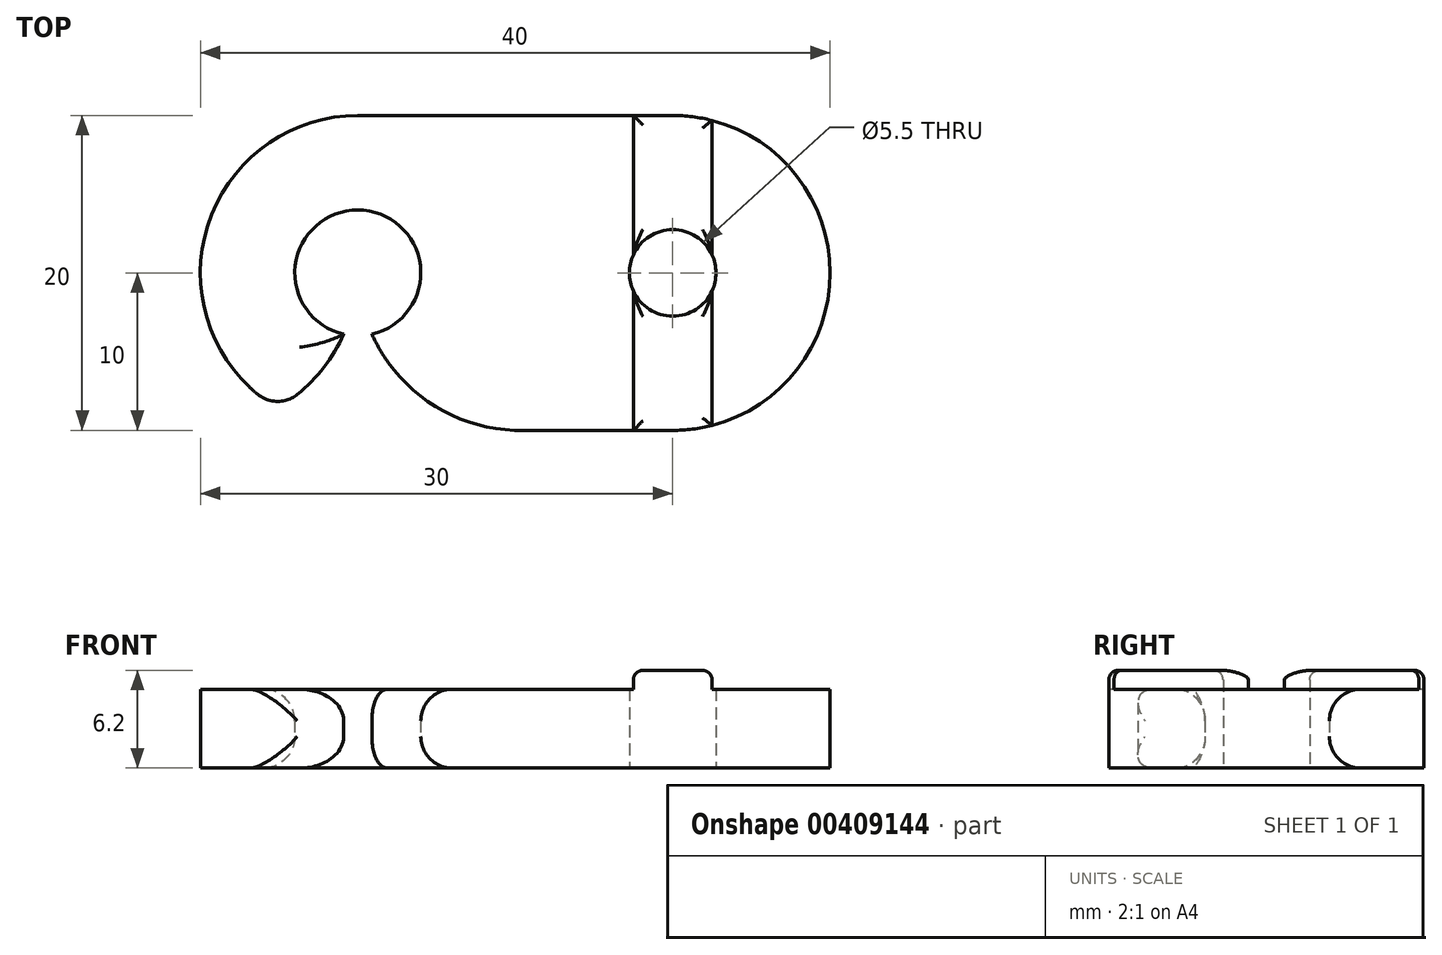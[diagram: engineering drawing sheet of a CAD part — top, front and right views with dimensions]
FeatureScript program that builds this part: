
annotation { "Feature Type Name" : "Feature", "Feature Type Description" : "" }
export const myFeature = defineFeature(function(context is Context, id is Id, definition is map)
    precondition{}
    {
        {
            var Q0;
            Q0=qCreatedBy(makeId("Top.planeOp"),FACE);
            var sketch = newSketch(context, id + "F0", { "sketchPlane" : qUnion([Q0])});
            skArc(sketch, "E0", {"start": v(10, -10) * mm, "mid": v(20, 0) * mm, "end": v(10, 10) * mm});
            skLineSegment(sketch, "E1", {"start": v(0, -10) * mm, "end": v(10, -10) * mm});
            skLineSegment(sketch, "E2", {"start": v(0, 10) * mm, "end": v(10, 10) * mm});
            skCircle(sketch, "E3", {"center": v(10, 0) * mm, "radius": 2.75 * mm});
            skArc(sketch, "E4.MirrorCS", {"start": v(-10, -10) * mm, "mid": v(-20, 0) * mm, "end": v(-10, 10) * mm});
            skLineSegment(sketch, "E5.MirrorCS", {"start": v(0, -10) * mm, "end": v(-10, -10) * mm});
            skCircle(sketch, "E6.MirrorC", {"center": v(-10, 0) * mm, "radius": 4 * mm});
            skLineSegment(sketch, "E7.MirrorCS", {"start": v(0, 10) * mm, "end": v(-10, 10) * mm});
            skLineSegment(sketch, "E8", {"start": v(-10, 0) * mm, "end": v(-10, -10) * mm, "construction": true});
            skLineSegment(sketch, "E9", {"start": v(-10, -3.9) * mm, "end": v(-9.1, -3.9) * mm, "construction": true});
            skArc(sketch, "E10", {"start": v(-10, 0) * mm, "mid": v(-6.98, -6.98) * mm, "end": v(0, -10) * mm});
            skArc(sketch, "E11.MirrorCS", {"start": v(-10, 0) * mm, "mid": v(-13.02, -6.98) * mm, "end": v(-20, -10) * mm});
            skSolve(sketch);
        }
        {
            var Q0;
            Q0=makeQuery(id+"F0.imprint","IMPRINT",FACE,{"disambiguationData":[TD([[makeQuery(id+"F0.imprint","IMPRINT",EDGE,{"derivedFrom":sQuery(id+"F0.wireOp",EDGE,"E0")}),1.0]])]});
            extrude(context, id + "F1", {"entities" : qUnion([Q0]), "depth" : 5 * mm, "offsetDistance" : 25 * mm});
        }
        {
            var Q0;
            Q0=makeQuery(id+"F1.opExtrude","CAP_FACE",FACE,{"disambiguationData":[OSD([sQuery(id+"F0.wireOp",EDGE,"E0"),sQuery(id+"F0.wireOp",EDGE,"E1"),sQuery(id+"F0.wireOp",EDGE,"E2"),sQuery(id+"F0.wireOp",EDGE,"E3"),sQuery(id+"F0.wireOp",EDGE,"E4.MirrorCS"),sQuery(id+"F0.wireOp",EDGE,"E6.MirrorC"),sQuery(id+"F0.wireOp",EDGE,"E7.MirrorCS"),sQuery(id+"F0.wireOp",EDGE,"E10"),sQuery(id+"F0.wireOp",EDGE,"E11.MirrorCS")])],"isStart":false});
            var sketch = newSketch(context, id + "F2", { "sketchPlane" : qUnion([Q0])});
            skCircle(sketch, "E12", {"center": v(10, 0) * mm, "radius": 2.5 * mm, "construction": true});
            skLineSegment(sketch, "E13", {"start": v(7.5, 10) * mm, "end": v(7.5, -10) * mm});
            skLineSegment(sketch, "E14", {"start": v(12.5, 9.68) * mm, "end": v(12.5, -9.68) * mm});
            skSolve(sketch);
        }
        {
            var Q0;
            {var subQ1=makeQuery(id+"F1.opExtrude","CAP_EDGE",EDGE,{"disambiguationData":[OSD([sQuery(id+"F0.wireOp",EDGE,"E0")])],"isStart":false});var subQ3=sQuery(id+"F2.wireOp",EDGE,"E14");var subQ4=makeQuery(id+"F2.imprint","INTERSECT",VERTEX,{"disambiguationData":[OD(0.0)],"derivedFrom":[subQ1,subQ3]});Q0=makeQuery(id+"F2.imprint","IMPRINT",FACE,{"disambiguationData":[TD([[makeQuery(id+"F2.imprint","IMPRINT",EDGE,{"disambiguationData":[TD([[subQ4,-1.0]])],"derivedFrom":subQ3}),-1.0]])]});}
            var Q1;
            {var subQ0=makeQuery(id+"F1.opExtrude","CAP_EDGE",EDGE,{"disambiguationData":[OSD([sQuery(id+"F0.wireOp",EDGE,"E1")])],"isStart":false});var subQ3=sQuery(id+"F2.wireOp",EDGE,"E13");var subQ4=makeQuery(id+"F2.imprint","INTERSECT",VERTEX,{"derivedFrom":[subQ0,subQ3]});Q1=makeQuery(id+"F2.imprint","IMPRINT",FACE,{"disambiguationData":[TD([[makeQuery(id+"F2.imprint","IMPRINT",EDGE,{"disambiguationData":[TD([[subQ4,1.0]])],"derivedFrom":subQ3}),1.0]])]});}
            extrude(context, id + "F3", {"entities" : qUnion([Q0, Q1]), "operationType" : NewBodyOperationType.ADD, "depth" : 1.2 * mm, "offsetDistance" : 25 * mm});
        }
        {
            var Q0;
            Q0=makeQuery(id+"F3.opExtrude","CAP_FACE",FACE,{"disambiguationData":[OSD([sQuery(id+"F0.wireOp",EDGE,"E0"),sQuery(id+"F0.wireOp",EDGE,"E2"),sQuery(id+"F0.wireOp",EDGE,"E3"),sQuery(id+"F0.wireOp",EDGE,"E7.MirrorCS"),sQuery(id+"F2.wireOp",EDGE,"E13"),sQuery(id+"F2.wireOp",EDGE,"E14")])],"isStart":false});
            var Q1;
            Q1=makeQuery(id+"F3.opExtrude","CAP_FACE",FACE,{"disambiguationData":[OSD([sQuery(id+"F0.wireOp",EDGE,"E0"),sQuery(id+"F0.wireOp",EDGE,"E1"),sQuery(id+"F0.wireOp",EDGE,"E3"),sQuery(id+"F2.wireOp",EDGE,"E13"),sQuery(id+"F2.wireOp",EDGE,"E14")])],"isStart":false});
            var Q2;
            {var subQ0=sQuery(id+"F2.wireOp",EDGE,"E13");Q2=makeQuery(id+"F3.opExtrude","CAP_EDGE",EDGE,{"disambiguationData":[OSD([subQ0]),TDD([makeQuery(id+"F2.imprint","IMPRINT",EDGE,{"disambiguationData":[TD([[makeQuery(id+"F2.imprint","INTERSECT",VERTEX,{"disambiguationData":[OD(0.0)],"derivedFrom":[makeQuery(id+"F1.opExtrude","CAP_EDGE",EDGE,{"disambiguationData":[OSD([sQuery(id+"F0.wireOp",EDGE,"E3")])],"isStart":false}),subQ0]}),1.0]])],"derivedFrom":subQ0})])],"isStart":true});}
            var Q3;
            {var subQ0=sQuery(id+"F2.wireOp",EDGE,"E14");Q3=makeQuery(id+"F3.opExtrude","CAP_EDGE",EDGE,{"disambiguationData":[OSD([subQ0]),TDD([makeQuery(id+"F2.imprint","IMPRINT",EDGE,{"disambiguationData":[TD([[makeQuery(id+"F2.imprint","INTERSECT",VERTEX,{"disambiguationData":[OD(0.0)],"derivedFrom":[makeQuery(id+"F1.opExtrude","CAP_EDGE",EDGE,{"disambiguationData":[OSD([sQuery(id+"F0.wireOp",EDGE,"E0")])],"isStart":false}),subQ0]}),-1.0]])],"derivedFrom":subQ0})])],"isStart":true});}
            fillet(context, id + "F4", {"entities" : qUnion([Q0, Q1, Q2, Q3]), "radius" : .6 * mm, "tangentPropagation" : true, "allowEdgeOverflow" : false});
        }
        {
            var Q0;
            Q0=makeQuery(id+"F1.opExtrude","CAP_EDGE",EDGE,{"disambiguationData":[OSD([sQuery(id+"F0.wireOp",EDGE,"E6.MirrorC")])],"isStart":false});
            var Q1;
            Q1=makeQuery(id+"F1.opExtrude","CAP_EDGE",EDGE,{"disambiguationData":[OSD([sQuery(id+"F0.wireOp",EDGE,"E6.MirrorC")])],"isStart":true});
            var Q2;
            Q2=makeQuery(id+"F1.opExtrude","SWEPT_EDGE",EDGE,{"disambiguationData":[OSD([sQuery(id+"F0.wireOp",EDGE,"E4.MirrorCS"),sQuery(id+"F0.wireOp",EDGE,"E11.MirrorCS")])]});
            var Q3;
            Q3=makeQuery(id+"F1.opExtrude","SWEPT_EDGE",EDGE,{"disambiguationData":[OSD([sQuery(id+"F0.wireOp",EDGE,"E1"),sQuery(id+"F0.wireOp",EDGE,"E5.MirrorCS"),sQuery(id+"F0.wireOp",EDGE,"E10")])]});
            var Q4;
            Q4=makeQuery(id+"F1.opExtrude","CAP_EDGE",EDGE,{"disambiguationData":[OSD([sQuery(id+"F0.wireOp",EDGE,"E11.MirrorCS")])],"isStart":true});
            var Q5;
            Q5=makeQuery(id+"F1.opExtrude","CAP_EDGE",EDGE,{"disambiguationData":[OSD([sQuery(id+"F0.wireOp",EDGE,"E11.MirrorCS")])],"isStart":false});
            fillet(context, id + "F5", {"entities" : qUnion([Q0, Q1, Q2, Q3, Q4, Q5]), "radius" : 2 * mm, "tangentPropagation" : true, "allowEdgeOverflow" : false});
        }
    });
